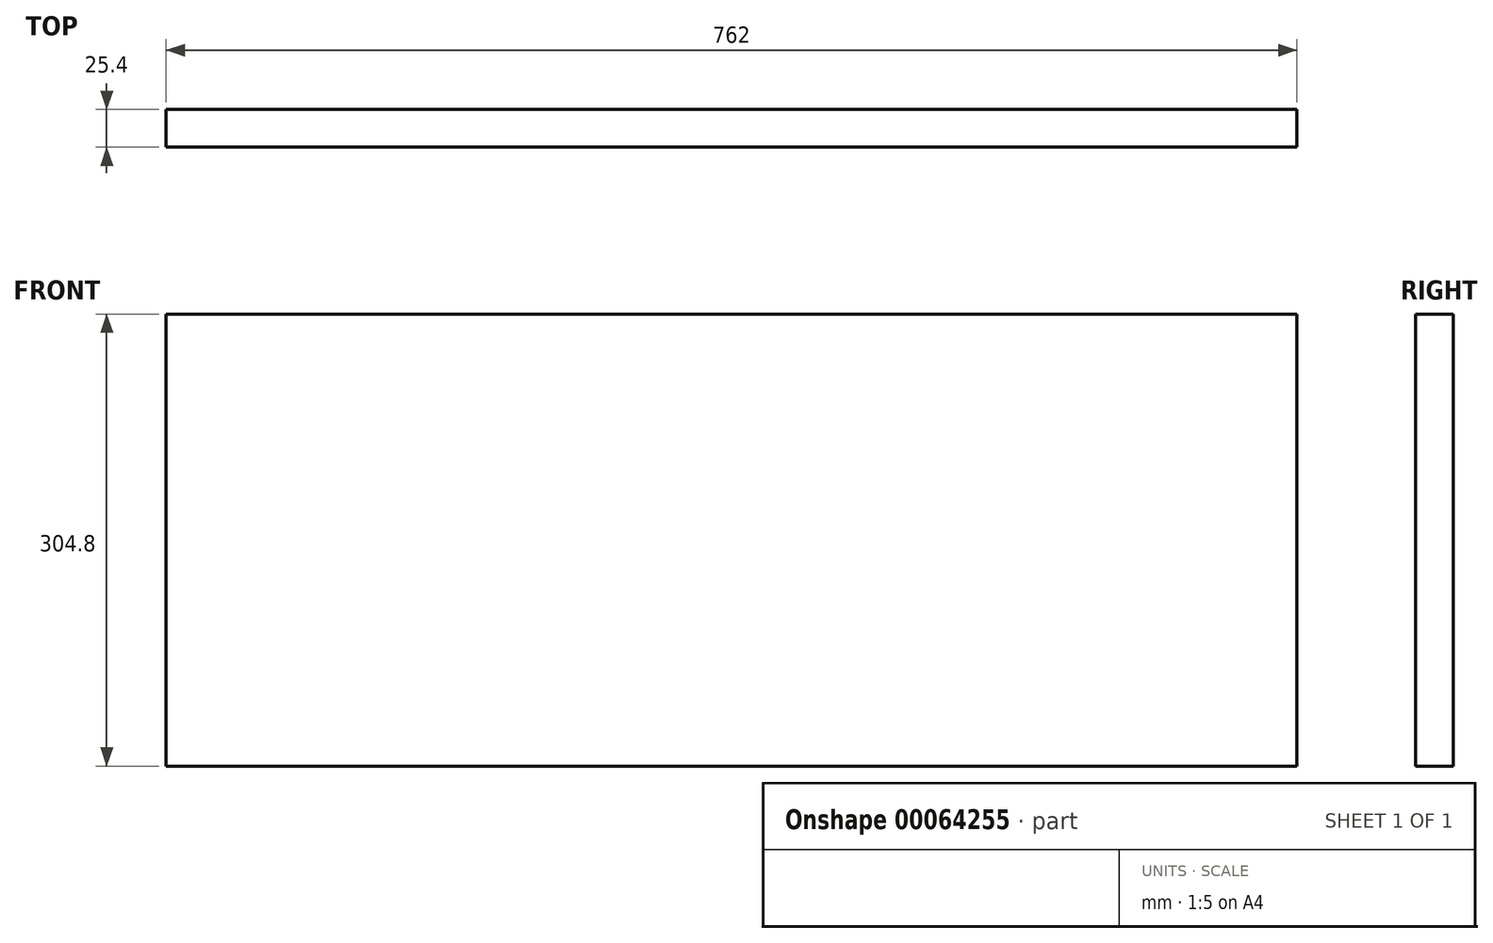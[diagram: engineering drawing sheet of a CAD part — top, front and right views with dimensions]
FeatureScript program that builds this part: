
annotation { "Feature Type Name" : "Feature", "Feature Type Description" : "" }
export const myFeature = defineFeature(function(context is Context, id is Id, definition is map)
    precondition{}
    {
        {
            var Q0;
            Q0=qCreatedBy(makeId("Front.planeOp"),FACE);
            var sketch = newSketch(context, id + "F0", { "sketchPlane" : qUnion([Q0])});
            skLineSegment(sketch, "E0.bottom", {"start": v(-380.75, 153.03) * mm, "end": v(381.25, 153.03) * mm});
            skLineSegment(sketch, "E0.top", {"start": v(-380.75, -151.77) * mm, "end": v(381.25, -151.77) * mm});
            skLineSegment(sketch, "E0.left", {"start": v(-380.75, 153.03) * mm, "end": v(-380.75, -151.77) * mm});
            skLineSegment(sketch, "E0.right", {"start": v(381.25, 153.03) * mm, "end": v(381.25, -151.77) * mm});
            skLineSegment(sketch, "E1", {"start": v(0, 0) * mm, "end": v(0.25, 153.03) * mm, "construction": true});
            skLineSegment(sketch, "E2", {"start": v(-380.75, 0.63) * mm, "end": v(0, 0) * mm, "construction": true});
            skSolve(sketch);
        }
        {
            var Q0;
            Q0=makeQuery(id+"F0.imprint","IMPRINT",FACE,{"disambiguationData":[TD([[makeQuery(id+"F0.imprint","IMPRINT",EDGE,{"derivedFrom":sQuery(id+"F0.wireOp",EDGE,"E0.bottom")}),-1.0]])]});
            extrude(context, id + "F1", {"entities" : qUnion([Q0]), "oppositeDirection" : true, "depth" : 25.4 * mm});
        }
    });
